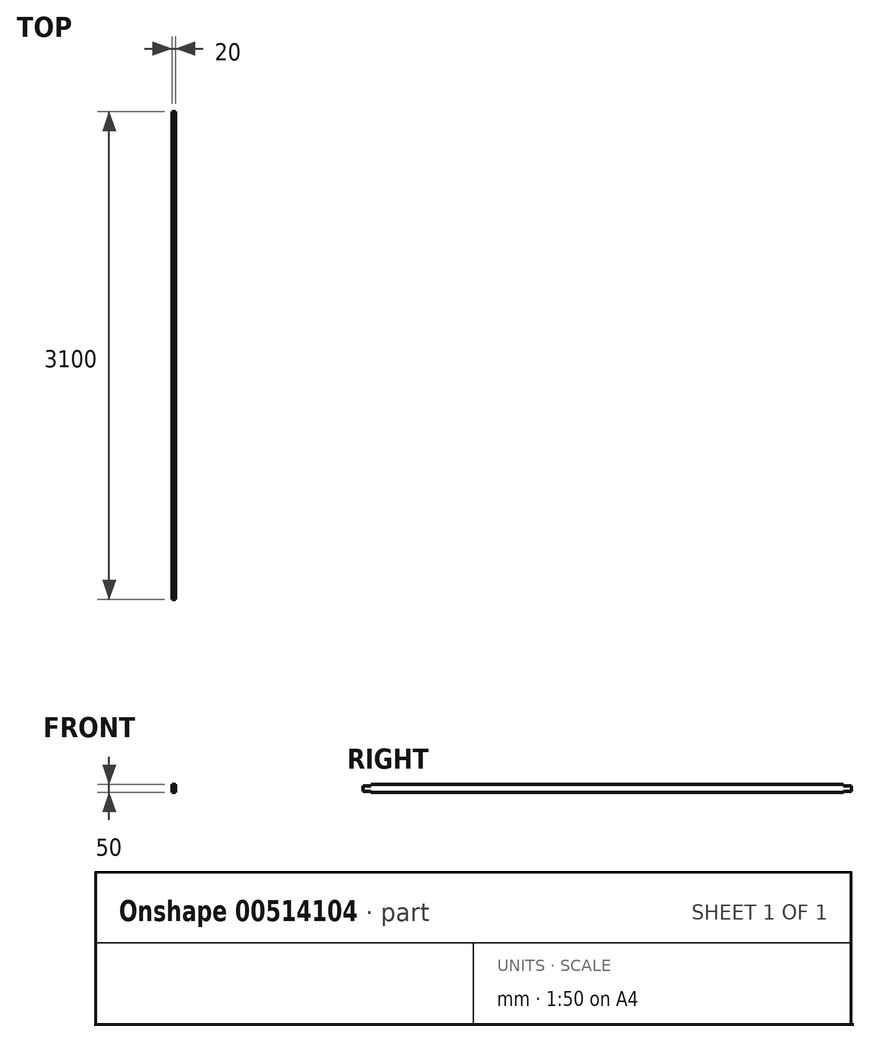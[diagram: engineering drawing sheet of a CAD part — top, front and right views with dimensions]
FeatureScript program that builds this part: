
annotation { "Feature Type Name" : "Feature", "Feature Type Description" : "" }
export const myFeature = defineFeature(function(context is Context, id is Id, definition is map)
    precondition{}
    {
        {
            var Q0;
            Q0=qCreatedBy(makeId("Front.planeOp"),FACE);
            var sketch = newSketch(context, id + "F0", { "sketchPlane" : qUnion([Q0])});
            skLineSegment(sketch, "E0.bottom", {"start": v(0, 0) * mm, "end": v(10, 0) * mm});
            skLineSegment(sketch, "E0.top", {"start": v(0, 50) * mm, "end": v(10, 50) * mm});
            skLineSegment(sketch, "E0.left", {"start": v(0, 0) * mm, "end": v(0, 50) * mm});
            skLineSegment(sketch, "E0.right", {"start": v(10, 0) * mm, "end": v(10, 50) * mm});
            skLineSegment(sketch, "E1.bottom", {"start": v(10, 50) * mm, "end": v(20, 50) * mm});
            skLineSegment(sketch, "E1.top", {"start": v(10, 0) * mm, "end": v(20, 0) * mm});
            skLineSegment(sketch, "E1.left", {"start": v(10, 50) * mm, "end": v(10, 0) * mm});
            skLineSegment(sketch, "E1.right", {"start": v(20, 50) * mm, "end": v(20, 0) * mm});
            skSolve(sketch);
        }
        {
            var Q0;
            Q0 = qSketchRegion(id + "F0", true);
            extrude(context, id + "F1", {"entities" : qUnion([Q0]), "depth" : 3000 * mm});
        }
        {
            var Q0;
            Q0=makeQuery(id+"F1.opExtrude","CAP_FACE",FACE,{"disambiguationData":[OSD([sQuery(id+"F0.wireOp",EDGE,"E0.bottom"),sQuery(id+"F0.wireOp",EDGE,"E0.top"),sQuery(id+"F0.wireOp",EDGE,"E0.left"),sQuery(id+"F0.wireOp",EDGE,"E1.bottom"),sQuery(id+"F0.wireOp",EDGE,"E1.top"),sQuery(id+"F0.wireOp",EDGE,"E1.right")])],"isStart":false});
            var sketch = newSketch(context, id + "F2", { "sketchPlane" : qUnion([Q0])});
            skCircle(sketch, "E2", {"center": v(10, 25) * mm, "radius": 20 * mm, "construction": true});
            skLineSegment(sketch, "E3.0", {"start": v(0, 0) * mm, "end": v(0, 50) * mm, "construction": true});
            skLineSegment(sketch, "E4.0", {"start": v(20, 50) * mm, "end": v(20, 0) * mm, "construction": true});
            skLineSegment(sketch, "E5", {"start": v(0, 7.68) * mm, "end": v(20, 7.68) * mm});
            skLineSegment(sketch, "E6", {"start": v(0, 42.32) * mm, "end": v(20, 42.32) * mm});
            skLineSegment(sketch, "E7", {"start": v(0, 7.68) * mm, "end": v(0, 42.32) * mm});
            skLineSegment(sketch, "E8", {"start": v(20, 7.68) * mm, "end": v(20, 42.32) * mm});
            skSolve(sketch);
        }
        {
            var Q0;
            Q0 = qSketchRegion(id + "F2", true);
            extrude(context, id + "F3", {"entities" : qUnion([Q0]), "operationType" : NewBodyOperationType.ADD, "depth" : 50 * mm});
        }
        {
            var Q0;
            Q0=makeQuery(id+"F1.opExtrude","CAP_FACE",FACE,{"disambiguationData":[OSD([sQuery(id+"F0.wireOp",EDGE,"E0.bottom"),sQuery(id+"F0.wireOp",EDGE,"E0.top"),sQuery(id+"F0.wireOp",EDGE,"E0.left"),sQuery(id+"F0.wireOp",EDGE,"E1.bottom"),sQuery(id+"F0.wireOp",EDGE,"E1.top"),sQuery(id+"F0.wireOp",EDGE,"E1.right")])],"isStart":true});
            var sketch = newSketch(context, id + "F4", { "sketchPlane" : qUnion([Q0])});
            skCircle(sketch, "E9", {"center": v(-10, 25) * mm, "radius": 20 * mm, "construction": true});
            skLineSegment(sketch, "E10.0", {"start": v(0, 0) * mm, "end": v(0, 50) * mm, "construction": true});
            skLineSegment(sketch, "E11.0", {"start": v(-20, 50) * mm, "end": v(-20, 0) * mm, "construction": true});
            skLineSegment(sketch, "E12.bottom", {"start": v(-20, 42.32) * mm, "end": v(0, 42.32) * mm});
            skLineSegment(sketch, "E12.top", {"start": v(-20, 7.68) * mm, "end": v(0, 7.68) * mm});
            skLineSegment(sketch, "E12.left", {"start": v(-20, 42.32) * mm, "end": v(-20, 7.68) * mm});
            skLineSegment(sketch, "E12.right", {"start": v(0, 42.32) * mm, "end": v(0, 7.68) * mm});
            skSolve(sketch);
        }
        {
            var Q0;
            Q0 = qSketchRegion(id + "F4", true);
            extrude(context, id + "F5", {"entities" : qUnion([Q0]), "operationType" : NewBodyOperationType.ADD, "depth" : 50 * mm});
        }
    });
